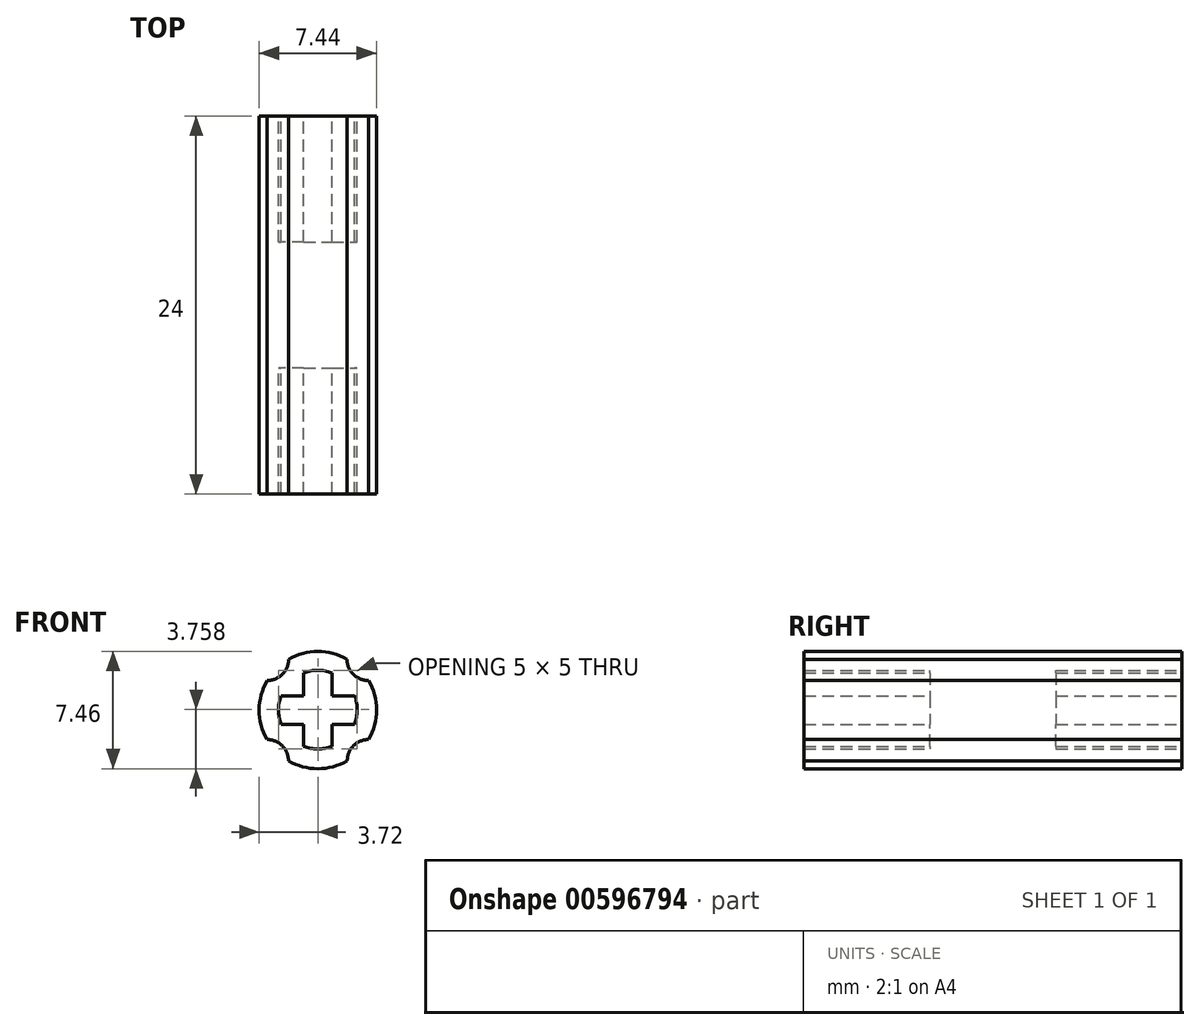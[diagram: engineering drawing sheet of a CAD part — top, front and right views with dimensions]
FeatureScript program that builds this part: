
annotation { "Feature Type Name" : "Feature", "Feature Type Description" : "" }
export const myFeature = defineFeature(function(context is Context, id is Id, definition is map)
    precondition{}
    {
        {
            var Q0;
            Q0=qCreatedBy(makeId("Front.planeOp"),FACE);
            var sketch = newSketch(context, id + "F0", { "sketchPlane" : qUnion([Q0])});
            skArc(sketch, "E0", {"start": v(-3.22, 1.88) * mm, "mid": v(-3.72, 0) * mm, "end": v(-3.22, -1.87) * mm});
            skCircle(sketch, "E1", {"center": v(0, 0) * mm, "radius": 3.2 * mm, "construction": true});
            skPoint(sketch, "E2.startSnap0", {"position": v(0, 0.03) * mm});
            skArc(sketch, "E3", {"start": v(1.85, 3.23) * mm, "mid": v(2.25, 2.27) * mm, "end": v(3.22, 1.88) * mm});
            skArc(sketch, "E4", {"start": v(-3.22, 1.88) * mm, "mid": v(-2.25, 2.27) * mm, "end": v(-1.85, 3.23) * mm});
            skArc(sketch, "E5", {"start": v(-1.87, -3.22) * mm, "mid": v(-2.26, -2.26) * mm, "end": v(-3.22, -1.87) * mm});
            skArc(sketch, "E6", {"start": v(3.22, -1.87) * mm, "mid": v(2.26, -2.26) * mm, "end": v(1.87, -3.22) * mm});
            skArc(sketch, "E7.trimOffspring", {"start": v(-1.87, -3.22) * mm, "mid": v(0, -3.72) * mm, "end": v(1.87, -3.22) * mm});
            skArc(sketch, "E8.trimOffspring", {"start": v(3.22, -1.87) * mm, "mid": v(3.72, 0) * mm, "end": v(3.22, 1.88) * mm});
            skPoint(sketch, "E9.orphan", {"position": v(0, 5.25) * mm});
            skPoint(sketch, "E10.orphan", {"position": v(-5.14, 0.03) * mm});
            skLineSegment(sketch, "E11.trimOffspring", {"start": v(0, 0.03) * mm, "end": v(0, 0) * mm});
            skPoint(sketch, "E12.trimOffspring.end.orphan", {"position": v(0, -5.2) * mm});
            skArc(sketch, "E13.trimOffspring", {"start": v(1.85, 3.23) * mm, "mid": v(0, 3.72) * mm, "end": v(-1.85, 3.23) * mm});
            skLineSegment(sketch, "E14", {"start": v(0, 0) * mm, "end": v(0, 0.9) * mm, "construction": true});
            skLineSegment(sketch, "E15", {"start": v(0, 0.9) * mm, "end": v(0, -0.9) * mm, "construction": true});
            skLineSegment(sketch, "E16", {"start": v(0, 0) * mm, "end": v(0.9, 0) * mm, "construction": true});
            skLineSegment(sketch, "E17", {"start": v(0.9, 0) * mm, "end": v(-0.9, 0) * mm, "construction": true});
            skLineSegment(sketch, "E18", {"start": v(-0.9, 2.36) * mm, "end": v(-0.9, 0.9) * mm});
            skLineSegment(sketch, "E19", {"start": v(-0.9, 0.9) * mm, "end": v(-2.34, 0.9) * mm});
            skLineSegment(sketch, "E20", {"start": v(-0.9, -2.3) * mm, "end": v(-0.9, -0.9) * mm});
            skLineSegment(sketch, "E21", {"start": v(-0.9, -0.9) * mm, "end": v(-2.32, -0.9) * mm});
            skLineSegment(sketch, "E22", {"start": v(0.9, 2.36) * mm, "end": v(0.9, 0.9) * mm});
            skLineSegment(sketch, "E23", {"start": v(0.9, 0.9) * mm, "end": v(2.34, 0.9) * mm});
            skLineSegment(sketch, "E24", {"start": v(0.9, -2.3) * mm, "end": v(0.9, -0.9) * mm});
            skLineSegment(sketch, "E25", {"start": v(0.9, -0.9) * mm, "end": v(2.32, -0.9) * mm});
            skCircle(sketch, "E26", {"center": v(0, 0.03) * mm, "radius": 2.5 * mm});
            skPoint(sketch, "E27.orphan", {"position": v(0.9, 3.07) * mm});
            skPoint(sketch, "E28.orphan", {"position": v(-0.9, 3.07) * mm});
            skPoint(sketch, "E29.orphan", {"position": v(-0.9, -3.07) * mm});
            skPoint(sketch, "E30.orphan", {"position": v(0.9, -3.07) * mm});
            skSolve(sketch);
        }
        {
            var Q0;
            {var subQ0=sQuery(id+"F0.wireOp",EDGE,"E24");Q0=makeQuery(id+"F0.imprint","IMPRINT",FACE,{"disambiguationData":[TD([[makeQuery(id+"F0.imprint","IMPRINT",EDGE,{"derivedFrom":subQ0}),-1.0]])]});}
            var Q1;
            Q1=makeQuery(id+"F0.imprint","IMPRINT",FACE,{"disambiguationData":[TD([[makeQuery(id+"F0.imprint","IMPRINT",EDGE,{"derivedFrom":sQuery(id+"F0.wireOp",EDGE,"E0")}),1.0]])]});
            var Q2;
            {var subQ0=sQuery(id+"F0.wireOp",EDGE,"E22");Q2=makeQuery(id+"F0.imprint","IMPRINT",FACE,{"disambiguationData":[TD([[makeQuery(id+"F0.imprint","IMPRINT",EDGE,{"derivedFrom":subQ0}),1.0]])]});}
            var Q3;
            {var subQ0=sQuery(id+"F0.wireOp",EDGE,"E18");Q3=makeQuery(id+"F0.imprint","IMPRINT",FACE,{"disambiguationData":[TD([[makeQuery(id+"F0.imprint","IMPRINT",EDGE,{"derivedFrom":subQ0}),-1.0]])]});}
            var Q4;
            {var subQ0=sQuery(id+"F0.wireOp",EDGE,"E20");Q4=makeQuery(id+"F0.imprint","IMPRINT",FACE,{"disambiguationData":[TD([[makeQuery(id+"F0.imprint","IMPRINT",EDGE,{"derivedFrom":subQ0}),1.0]])]});}
            extrude(context, id + "F1", {"entities" : qUnion([Q0, Q1, Q2, Q3, Q4]), "endBound" : BoundingType.SYMMETRIC, "depth" : 24 * mm, "offsetDistance" : 25 * mm});
        }
        {
            var Q0;
            {var subQ1=sQuery(id+"F0.wireOp",EDGE,"E18");Q0=makeQuery(id+"F0.imprint","IMPRINT",FACE,{"disambiguationData":[TD([[makeQuery(id+"F0.imprint","IMPRINT",EDGE,{"derivedFrom":subQ1}),1.0]])]});}
            extrude(context, id + "F2", {"entities" : qUnion([Q0]), "operationType" : NewBodyOperationType.ADD, "endBound" : BoundingType.SYMMETRIC, "depth" : 8 * mm, "offsetDistance" : 25 * mm});
        }
    });
